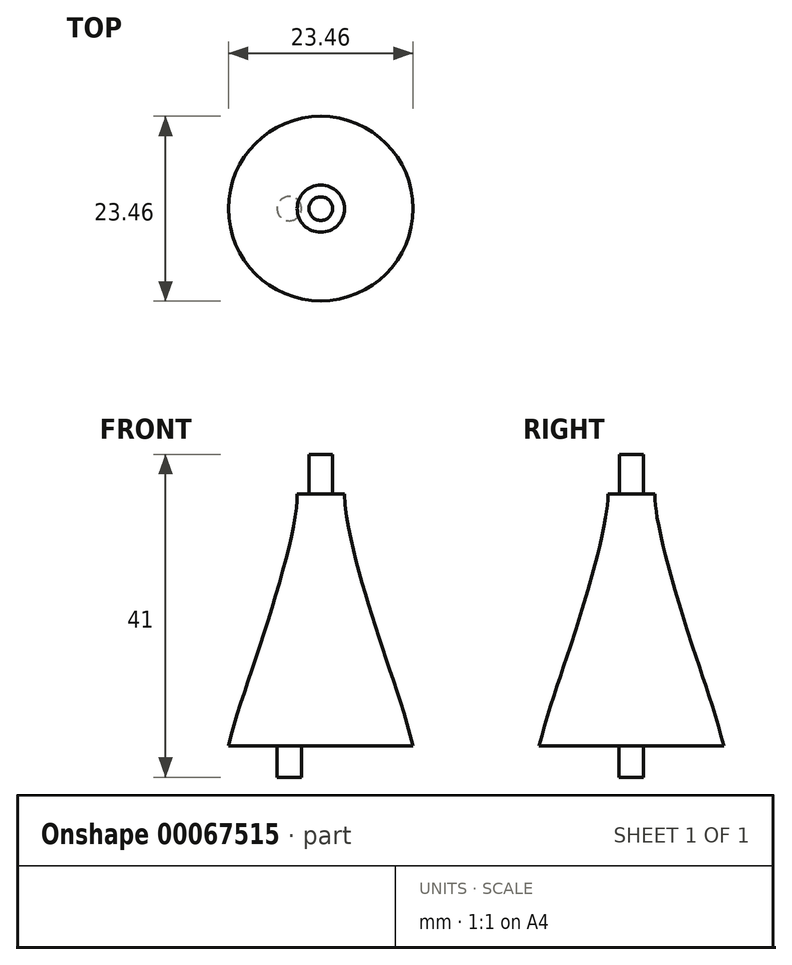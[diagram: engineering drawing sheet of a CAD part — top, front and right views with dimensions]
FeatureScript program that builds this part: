
annotation { "Feature Type Name" : "Feature", "Feature Type Description" : "" }
export const myFeature = defineFeature(function(context is Context, id is Id, definition is map)
    precondition{}
    {
        {
            var Q0;
            Q0=qCreatedBy(makeId("Top.planeOp"),FACE);
            var sketch = newSketch(context, id + "F0", { "sketchPlane" : qUnion([Q0])});
            skCircle(sketch, "E0", {"center": v(0, 0) * mm, "radius": 12.5 * mm});
            skCircle(sketch, "E1", {"center": v(4, 0) * mm, "radius": 1.55 * mm});
            skCircle(sketch, "E2.MirrorC", {"center": v(-4, 0) * mm, "radius": 1.55 * mm});
            skSolve(sketch);
        }
        {
            var Q0;
            Q0=qCreatedBy(makeId("Front.planeOp"),FACE);
            var sketch = newSketch(context, id + "F1", { "sketchPlane" : qUnion([Q0])});
            skLineSegment(sketch, "E3", {"start": v(0, 0) * mm, "end": v(12.5, 0) * mm});
            skLineSegment(sketch, "E4", {"start": v(0, 0) * mm, "end": v(0, 36) * mm});
            skLineSegment(sketch, "E5", {"start": v(0, 36) * mm, "end": v(3, 36) * mm});
            skFitSpline(sketch, "E6", {"points": [v(3, 36) * mm, v(7.2, 18.34) * mm, v(12.5, 0) * mm], "startDerivative": vector(-0.56, -20.02) * mm, "endDerivative": vector(3.92, -30.64) * mm});
            skSolve(sketch);
        }
        {
            var Q0;
            Q0=makeQuery(id+"F1.imprint","IMPRINT",FACE,{"disambiguationData":[TD([[makeQuery(id+"F1.imprint","IMPRINT",EDGE,{"derivedFrom":sQuery(id+"F1.wireOp",EDGE,"E3")}),1.0]])]});
            var Q1;
            Q1=sQuery(id+"F1.wireOp",EDGE,"E4");
            revolve(context, id + "F2", {"entities" : qUnion([Q0]), "axis" : qUnion([Q1]), "revolveType" : RevolveType.FULL});
        }
        {
            var Q0;
            Q0=makeQuery(id+"F2.opRevolve","SWEPT_FACE",FACE,{"disambiguationData":[OSD([sQuery(id+"F1.wireOp",EDGE,"E5")])]});
            var sketch = newSketch(context, id + "F3", { "sketchPlane" : qUnion([Q0])});
            skCircle(sketch, "E7", {"center": v(0, 0) * mm, "radius": 1.5 * mm});
            skSolve(sketch);
        }
        {
            var Q0;
            Q0=makeQuery(id+"F3.imprint","IMPRINT",FACE,{"disambiguationData":[TD([[makeQuery(id+"F3.imprint","IMPRINT",EDGE,{"derivedFrom":sQuery(id+"F3.wireOp",EDGE,"E7")}),1.0]])]});
            extrude(context, id + "F4", {"entities" : qUnion([Q0]), "operationType" : NewBodyOperationType.ADD, "depth" : 5 * mm});
        }
        {
            var Q0;
            Q0=makeQuery(id+"F0.imprint","IMPRINT",FACE,{"disambiguationData":[TD([[makeQuery(id+"F0.imprint","IMPRINT",EDGE,{"derivedFrom":sQuery(id+"F0.wireOp",EDGE,"E1")}),1.0]])]});
            var Q1;
            Q1=makeQuery(id+"F0.imprint","IMPRINT",FACE,{"disambiguationData":[TD([[makeQuery(id+"F0.imprint","IMPRINT",EDGE,{"derivedFrom":sQuery(id+"F0.wireOp",EDGE,"E2.MirrorC")}),-1.0]])]});
            extrude(context, id + "F5", {"entities" : qUnion([Q0, Q1]), "operationType" : NewBodyOperationType.REMOVE, "depth" : 4 * mm});
        }
    });
